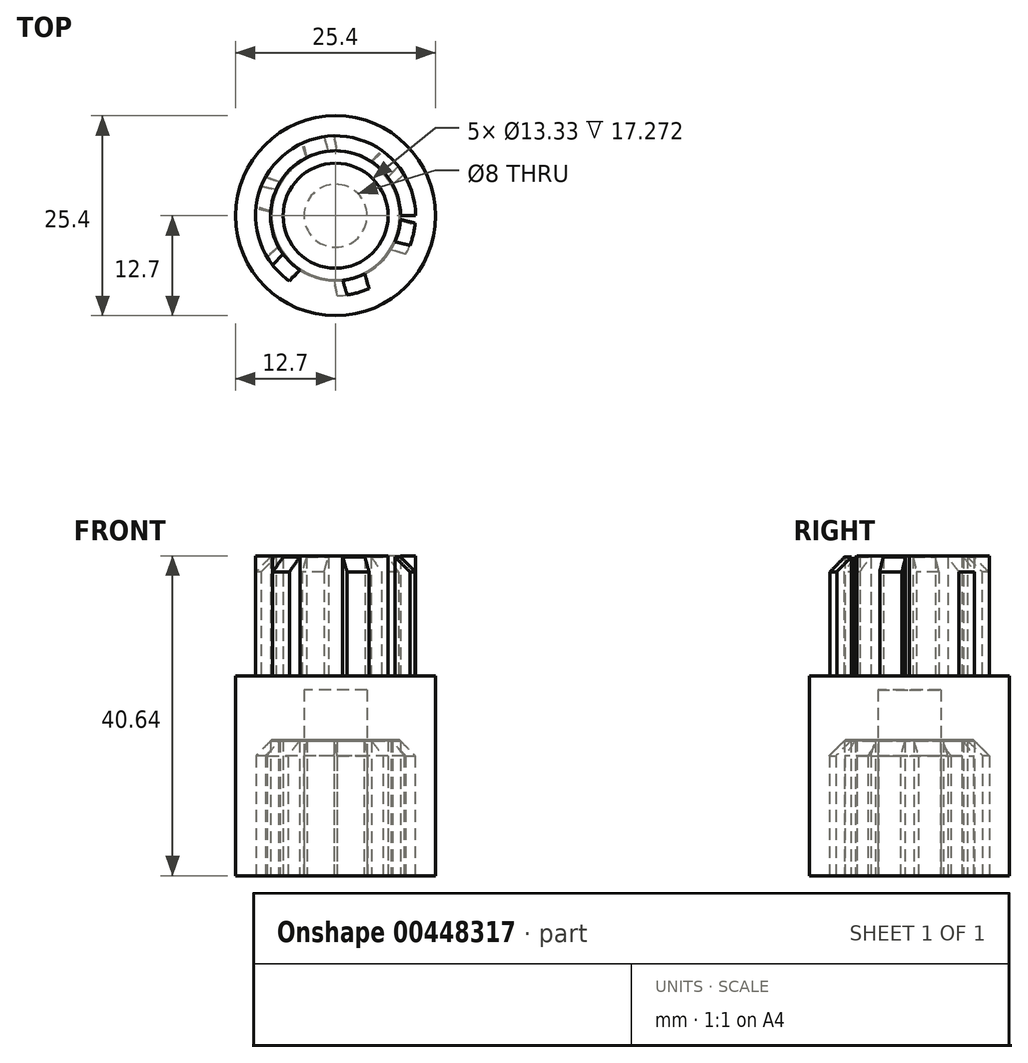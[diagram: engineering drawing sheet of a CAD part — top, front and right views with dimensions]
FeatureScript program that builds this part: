
annotation { "Feature Type Name" : "Feature", "Feature Type Description" : "" }
export const myFeature = defineFeature(function(context is Context, id is Id, definition is map)
    precondition{}
    {
        {
            var Q0;
            Q0=qCreatedBy(makeId("Top.planeOp"),FACE);
            var sketch = newSketch(context, id + "F0", { "sketchPlane" : qUnion([Q0])});
            skCircle(sketch, "E0", {"center": v(0, 0) * mm, "radius": 8.26 * mm});
            skCircle(sketch, "E1", {"center": v(0, 0) * mm, "radius": 10.16 * mm});
            skCircle(sketch, "E2", {"center": v(0, 0) * mm, "radius": 6.67 * mm});
            skLineSegment(sketch, "E3", {"start": v(-4.6, -6.86) * mm, "end": v(-6.04, -8.17) * mm});
            skLineSegment(sketch, "E4", {"start": v(-7.25, -3.95) * mm, "end": v(-8.7, -5.26) * mm});
            skCircle(sketch, "E5", {"center": v(0, 0) * mm, "radius": 4 * mm});
            skLineSegment(sketch, "E6", {"start": v(0, 0) * mm, "end": v(-11.07, -10.1) * mm, "construction": true});
            skSolve(sketch);
        }
        {
            var Q0;
            Q0=makeQuery(id+"F0.imprint","IMPRINT",FACE,{"disambiguationData":[TD([[makeQuery(id+"F0.imprint","IMPRINT",EDGE,{"derivedFrom":sQuery(id+"F0.wireOp",EDGE,"E0")}),1.0]])]});
            extrude(context, id + "F1", {"entities" : qUnion([Q0]), "depth" : 17.27 * mm});
        }
        {
            var Q0;
            {var subQ0=sQuery(id+"F0.wireOp",EDGE,"E3");Q0=makeQuery(id+"F0.imprint","IMPRINT",FACE,{"disambiguationData":[TD([[makeQuery(id+"F0.imprint","IMPRINT",EDGE,{"derivedFrom":subQ0}),-1.0]])]});}
            extrude(context, id + "F2", {"entities" : qUnion([Q0]), "operationType" : NewBodyOperationType.ADD, "depth" : 17.27 * mm});
        }
        {
            var Q0;
            Q0=makeQuery(id+"F2.opExtrude","CAP_EDGE",EDGE,{"disambiguationData":[OSD([sQuery(id+"F0.wireOp",EDGE,"E1")])],"isStart":false});
            chamfer(context, id + "F3", {"entities" : qUnion([Q0]), "width" : 2.03 * mm, "tangentPropagation" : true});
        }
        {
            var Q0;
            Q0=makeQuery(id+"F1.opExtrude","SWEPT_BODY",BODY,{"disambiguationData":[OSD([sQuery(id+"F0.wireOp",EDGE,"E0"),sQuery(id+"F0.wireOp",EDGE,"E2")])]});
            var Q1;
            Q1=makeQuery(id+"F1.opExtrude","SWEPT_FACE",FACE,{"disambiguationData":[OSD([sQuery(id+"F0.wireOp",EDGE,"E0")])]});
            circularPattern(context, id + "F4", {"entities" : qUnion([Q0]), "axis" : qUnion([Q1]), "angle" : 360 * degree, "instanceCount" : 6, "equalSpace" : true});
        }
        {
            var Q0;
            Q0=makeQuery(id+"F0.imprint","IMPRINT",FACE,{"disambiguationData":[TD([[makeQuery(id+"F0.imprint","IMPRINT",EDGE,{"derivedFrom":sQuery(id+"F0.wireOp",EDGE,"E5")}),1.0]])]});
            extrude(context, id + "F5", {"entities" : qUnion([Q0]), "depth" : 23.62 * mm});
        }
        {
            var Q0;
            Q0=makeQuery(id+"F0.imprint","IMPRINT",FACE,{"disambiguationData":[TD([[makeQuery(id+"F0.imprint","IMPRINT",EDGE,{"derivedFrom":sQuery(id+"F0.wireOp",EDGE,"E2")}),1.0]])]});
            extrude(context, id + "F6", {"entities" : qUnion([Q0]), "depth" : 15.24 * mm});
        }
        {
            var Q0;
            Q0=qCreatedBy(makeId("Top.planeOp"),FACE);
            var sketch = newSketch(context, id + "F7", { "sketchPlane" : qUnion([Q0])});
            skCircle(sketch, "E7", {"center": v(0, 0) * mm, "radius": 12.7 * mm});
            skSolve(sketch);
        }
        {
            var Q0;
            Q0=makeQuery(id+"F7.imprint","IMPRINT",FACE,{"disambiguationData":[TD([[makeQuery(id+"F7.imprint","IMPRINT",EDGE,{"derivedFrom":sQuery(id+"F7.wireOp",EDGE,"E7")}),1.0]])]});
            extrude(context, id + "F8", {"entities" : qUnion([Q0]), "depth" : 25.4 * mm});
        }
        {
            var Q0;
            Q0=makeQuery(id+"F4.opPattern","COPY",BODY,{"derivedFrom":makeQuery(id+"F1.opExtrude","SWEPT_BODY",BODY,{"disambiguationData":[OSD([sQuery(id+"F0.wireOp",EDGE,"E0"),sQuery(id+"F0.wireOp",EDGE,"E2")])]}),"instanceName":"3"});
            var Q1;
            Q1=makeQuery(id+"F8.opExtrude","SWEPT_BODY",BODY,{"disambiguationData":[OSD([sQuery(id+"F7.wireOp",EDGE,"E7")])]});
            booleanBodies(context, id + "F9", {"operationType" : BooleanOperationType.SUBTRACTION, "tools" : qUnion([Q0]), "targets" : qUnion([Q1])});
        }
        {
            var Q0;
            Q0=makeQuery(id+"F8.opExtrude","CAP_FACE",FACE,{"disambiguationData":[OSD([sQuery(id+"F7.wireOp",EDGE,"E7")])],"isStart":false});
            var sketch = newSketch(context, id + "F10", { "sketchPlane" : qUnion([Q0])});
            skLineSegment(sketch, "E8", {"start": v(12.7, 0) * mm, "end": v(-12.7, 0) * mm});
            skPoint(sketch, "E9", {"position": v(0, 0) * mm});
            skCircle(sketch, "E10", {"center": v(0, 0) * mm, "radius": 8.26 * mm});
            skCircle(sketch, "E11", {"center": v(0, 0) * mm, "radius": 10.16 * mm});
            skCircle(sketch, "E12", {"center": v(0, 0) * mm, "radius": 6.67 * mm});
            skLineSegment(sketch, "E13", {"start": v(-4.53, -6.9) * mm, "end": v(-5.86, -8.3) * mm});
            skLineSegment(sketch, "E14", {"start": v(-6.65, -4.9) * mm, "end": v(-7.98, -6.3) * mm});
            skCircle(sketch, "E15", {"center": v(0, 0) * mm, "radius": 4 * mm});
            skLineSegment(sketch, "E16", {"start": v(0, 0) * mm, "end": v(-19.04, -20.08) * mm, "construction": true});
            skSolve(sketch);
        }
        {
            var Q0;
            {var subQ0=sQuery(id+"F10.wireOp",EDGE,"E15");var subQ1=sQuery(id+"F10.wireOp",EDGE,"E8");var subQ2=makeQuery(id+"F10.imprint","INTERSECT",VERTEX,{"disambiguationData":[OD(0.0)],"derivedFrom":[subQ1,subQ0]});Q0=makeQuery(id+"F10.imprint","IMPRINT",FACE,{"disambiguationData":[TD([[makeQuery(id+"F10.imprint","IMPRINT",EDGE,{"disambiguationData":[TD([[subQ2,-1.0]])],"derivedFrom":subQ1}),-1.0]])]});}
            var Q1;
            {var subQ0=sQuery(id+"F10.wireOp",EDGE,"E15");var subQ1=sQuery(id+"F10.wireOp",EDGE,"E8");var subQ2=makeQuery(id+"F10.imprint","INTERSECT",VERTEX,{"disambiguationData":[OD(0.0)],"derivedFrom":[subQ1,subQ0]});Q1=makeQuery(id+"F10.imprint","IMPRINT",FACE,{"disambiguationData":[TD([[makeQuery(id+"F10.imprint","IMPRINT",EDGE,{"disambiguationData":[TD([[subQ2,-1.0]])],"derivedFrom":subQ1}),1.0]])]});}
            var Q2;
            {var subQ0=sQuery(id+"F10.wireOp",EDGE,"E12");var subQ1=sQuery(id+"F10.wireOp",EDGE,"E8");var subQ2=makeQuery(id+"F10.imprint","INTERSECT",VERTEX,{"disambiguationData":[OD(0.0)],"derivedFrom":[subQ1,subQ0]});Q2=makeQuery(id+"F10.imprint","IMPRINT",FACE,{"disambiguationData":[TD([[makeQuery(id+"F10.imprint","IMPRINT",EDGE,{"disambiguationData":[TD([[subQ2,-1.0]])],"derivedFrom":subQ1}),1.0]])]});}
            var Q3;
            {var subQ0=sQuery(id+"F10.wireOp",EDGE,"E12");var subQ1=sQuery(id+"F10.wireOp",EDGE,"E8");var subQ2=makeQuery(id+"F10.imprint","INTERSECT",VERTEX,{"disambiguationData":[OD(0.0)],"derivedFrom":[subQ1,subQ0]});Q3=makeQuery(id+"F10.imprint","IMPRINT",FACE,{"disambiguationData":[TD([[makeQuery(id+"F10.imprint","IMPRINT",EDGE,{"disambiguationData":[TD([[subQ2,-1.0]])],"derivedFrom":subQ1}),-1.0]])]});}
            var Q4;
            {var subQ0=sQuery(id+"F10.wireOp",EDGE,"E10");var subQ1=sQuery(id+"F10.wireOp",EDGE,"E8");var subQ2=makeQuery(id+"F10.imprint","INTERSECT",VERTEX,{"disambiguationData":[OD(0.0)],"derivedFrom":[subQ1,subQ0]});Q4=makeQuery(id+"F10.imprint","IMPRINT",FACE,{"disambiguationData":[TD([[makeQuery(id+"F10.imprint","IMPRINT",EDGE,{"disambiguationData":[TD([[subQ2,-1.0]])],"derivedFrom":subQ1}),-1.0]])]});}
            var Q5;
            {var subQ0=sQuery(id+"F10.wireOp",EDGE,"E10");var subQ2=sQuery(id+"F10.wireOp",EDGE,"E8");var subQ7=makeQuery(id+"F10.imprint","INTERSECT",VERTEX,{"disambiguationData":[OD(0.0)],"derivedFrom":[subQ2,subQ0]});Q5=makeQuery(id+"F10.imprint","IMPRINT",FACE,{"disambiguationData":[TD([[makeQuery(id+"F10.imprint","IMPRINT",EDGE,{"disambiguationData":[TD([[subQ7,-1.0]])],"derivedFrom":subQ2}),1.0]])]});}
            var Q6;
            Q6=sQuery(id+"F10.wireOp",EDGE,"E15");
            var Q7;
            Q7=sQuery(id+"F10.wireOp",EDGE,"E12");
            var Q8;
            Q8=sQuery(id+"F10.wireOp",EDGE,"E10");
            extrude(context, id + "F11", {"entities" : qUnion([Q0, Q1, Q2, Q3, Q4, Q5]), "operationType" : NewBodyOperationType.ADD, "surfaceEntities" : qUnion([Q6, Q7, Q8]), "depth" : 15.24 * mm});
        }
        {
            var Q0;
            {var subQ0=sQuery(id+"F10.wireOp",EDGE,"E13");Q0=makeQuery(id+"F10.imprint","IMPRINT",FACE,{"disambiguationData":[TD([[makeQuery(id+"F10.imprint","IMPRINT",EDGE,{"derivedFrom":subQ0}),-1.0]])]});}
            extrude(context, id + "F12", {"entities" : qUnion([Q0]), "depth" : 15.24 * mm});
        }
        {
            var Q0;
            Q0=makeQuery(id+"F12.opExtrude","CAP_EDGE",EDGE,{"disambiguationData":[OSD([sQuery(id+"F10.wireOp",EDGE,"E11")])],"isStart":false});
            chamfer(context, id + "F13", {"entities" : qUnion([Q0]), "width" : 2.03 * mm, "tangentPropagation" : true});
        }
        {
            var Q0;
            Q0=makeQuery(id+"F12.opExtrude","SWEPT_BODY",BODY,{"disambiguationData":[OSD([sQuery(id+"F10.wireOp",EDGE,"E10"),sQuery(id+"F10.wireOp",EDGE,"E11"),sQuery(id+"F10.wireOp",EDGE,"E13"),sQuery(id+"F10.wireOp",EDGE,"E14")])]});
            var Q1;
            Q1=makeQuery(id+"F11.opExtrude","SWEPT_FACE",FACE,{"disambiguationData":[OSD([sQuery(id+"F10.wireOp",EDGE,"E10")])]});
            circularPattern(context, id + "F14", {"entities" : qUnion([Q0]), "axis" : qUnion([Q1]), "angle" : 360 * degree, "instanceCount" : 6, "equalSpace" : true});
        }
    });
